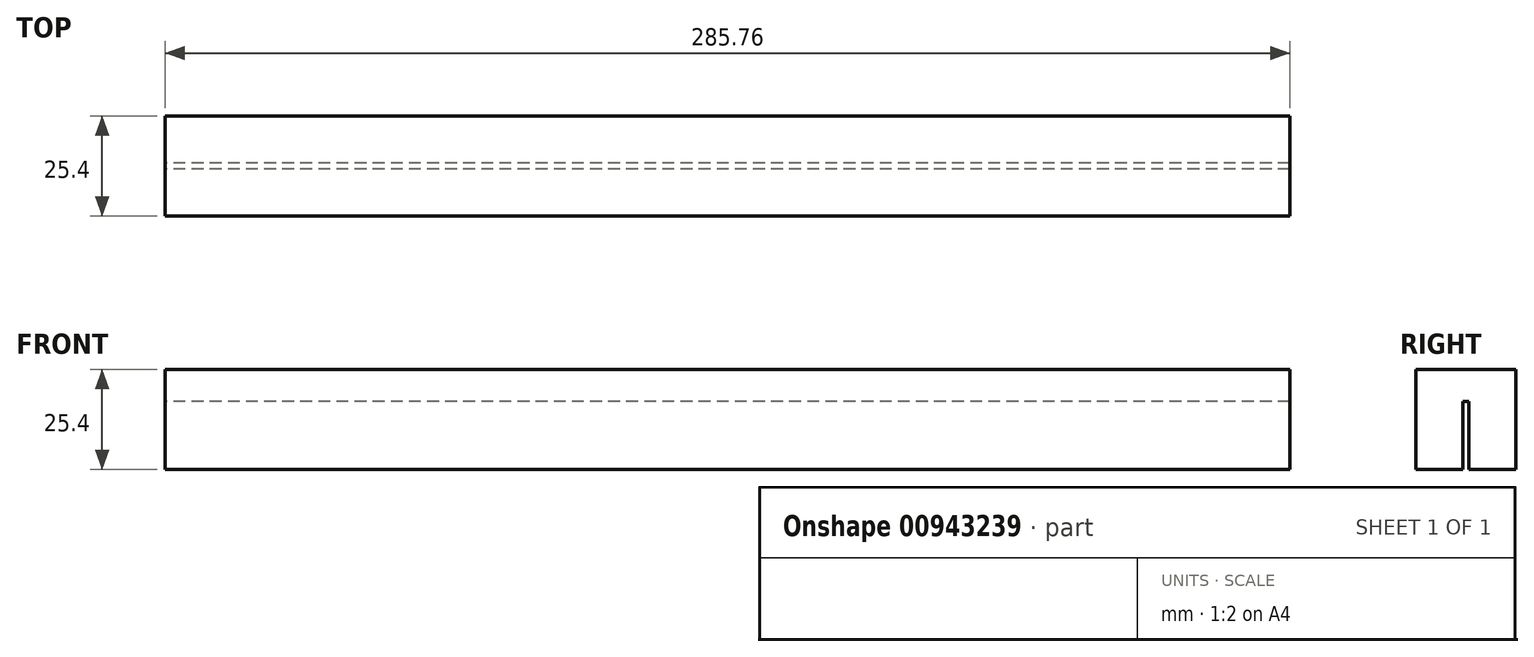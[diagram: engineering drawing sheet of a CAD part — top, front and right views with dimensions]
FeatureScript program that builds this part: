
annotation { "Feature Type Name" : "Feature", "Feature Type Description" : "" }
export const myFeature = defineFeature(function(context is Context, id is Id, definition is map)
    precondition{}
    {
        {
            var Q0;
            Q0=qCreatedBy(makeId("Right.planeOp"),FACE);
            var sketch = newSketch(context, id + "F0", { "sketchPlane" : qUnion([Q0])});
            skLineSegment(sketch, "E0.bottom", {"start": v(-12.7, 12.7) * mm, "end": v(12.7, 12.7) * mm});
            skLineSegment(sketch, "E0.top", {"start": v(-12.7, -12.7) * mm, "end": v(-0.8, -12.7) * mm});
            skLineSegment(sketch, "E0.left", {"start": v(-12.7, 12.7) * mm, "end": v(-12.7, -12.7) * mm});
            skLineSegment(sketch, "E0.right", {"start": v(12.7, 12.7) * mm, "end": v(12.7, -12.7) * mm});
            skLineSegment(sketch, "E1", {"start": v(-12.7, -12.7) * mm, "end": v(12.7, 12.7) * mm, "construction": true});
            skLineSegment(sketch, "E2.top", {"start": v(-0.8, 4.57) * mm, "end": v(0.8, 4.57) * mm});
            skLineSegment(sketch, "E2.left", {"start": v(-0.8, -12.7) * mm, "end": v(-0.8, 4.57) * mm});
            skLineSegment(sketch, "E2.right", {"start": v(0.8, -12.7) * mm, "end": v(0.8, 4.57) * mm});
            skLineSegment(sketch, "E3", {"start": v(0, 0) * mm, "end": v(0, 4.57) * mm, "construction": true});
            skLineSegment(sketch, "E4.trimOffspring", {"start": v(0.8, -12.7) * mm, "end": v(12.7, -12.7) * mm});
            skSolve(sketch);
        }
        {
            var Q0;
            Q0 = qSketchRegion(id + "F0", true);
            extrude(context, id + "F1", {"entities" : qUnion([Q0]), "endBound" : BoundingType.SYMMETRIC, "depth" : 285.75 * mm, "offsetDistance" : 25.4 * mm});
        }
    });
